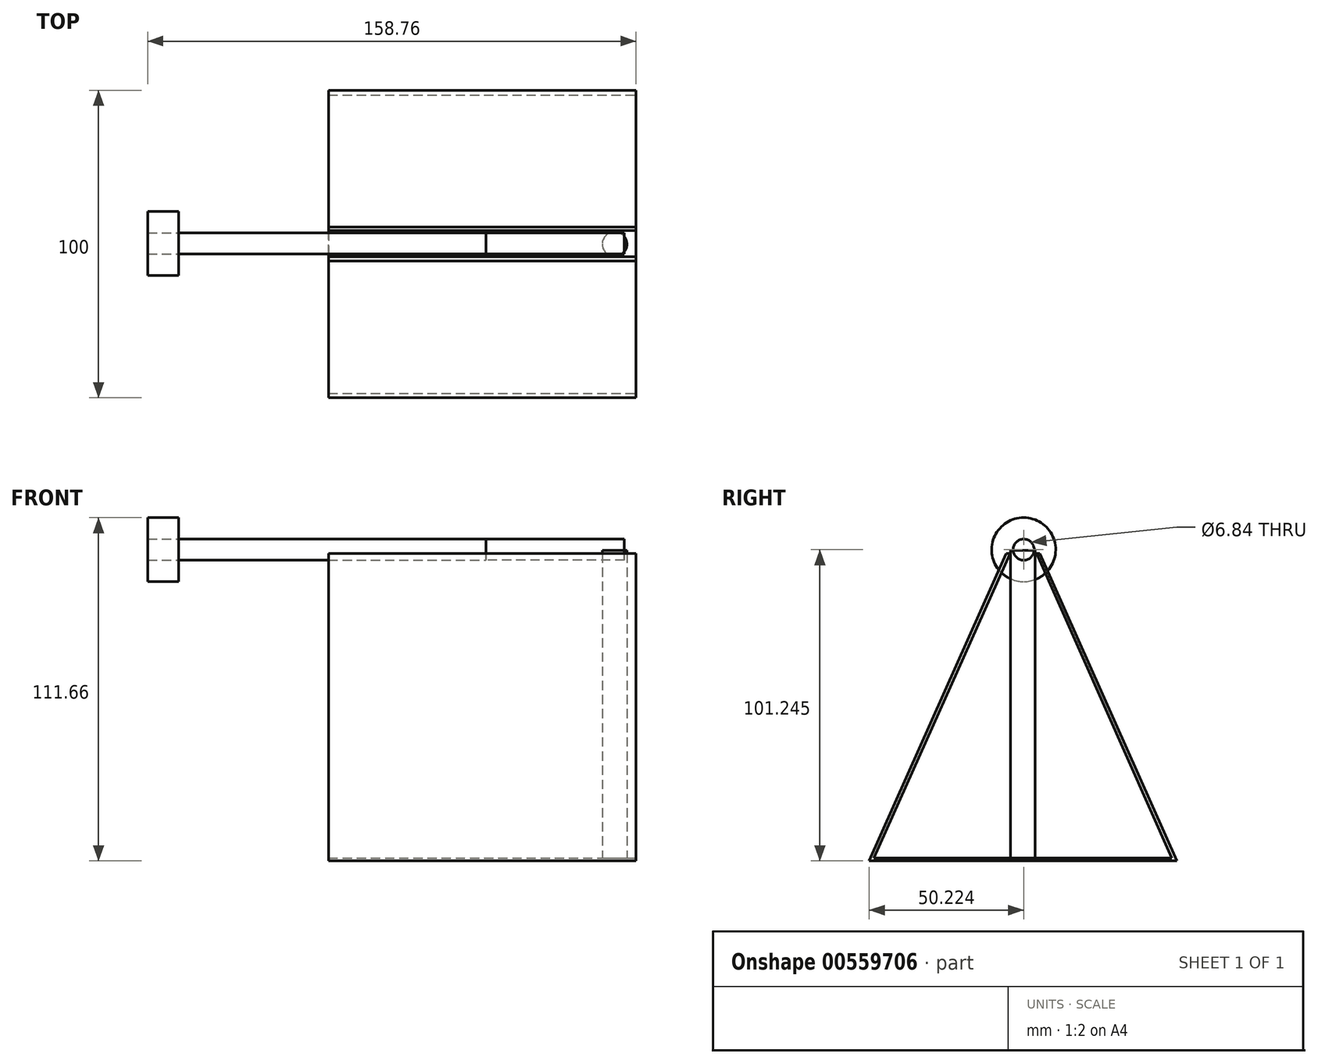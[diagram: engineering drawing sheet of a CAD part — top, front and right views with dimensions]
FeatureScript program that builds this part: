
annotation { "Feature Type Name" : "Feature", "Feature Type Description" : "" }
export const myFeature = defineFeature(function(context is Context, id is Id, definition is map)
    precondition{}
    {
        {
            var Q0;
            Q0=qCreatedBy(makeId("Front.planeOp"),FACE);
            var sketch = newSketch(context, id + "F0", { "sketchPlane" : qUnion([Q0])});
            skLineSegment(sketch, "E0.bottom", {"start": v(-51.24, 0) * mm, "end": v(48.76, 0) * mm});
            skLineSegment(sketch, "E0.top", {"start": v(-51.24, 100) * mm, "end": v(48.76, 100) * mm});
            skLineSegment(sketch, "E0.left", {"start": v(-51.24, 0) * mm, "end": v(-51.24, 100) * mm});
            skLineSegment(sketch, "E0.right", {"start": v(48.76, 0) * mm, "end": v(48.76, 100) * mm});
            skSolve(sketch);
        }
        {
            var Q0;
            Q0=makeQuery(id+"F0.imprint","IMPRINT",FACE,{"disambiguationData":[TD([[makeQuery(id+"F0.imprint","IMPRINT",EDGE,{"derivedFrom":sQuery(id+"F0.wireOp",EDGE,"E0.bottom")}),1.0]])]});
            extrude(context, id + "F1", {"entities" : qUnion([Q0]), "oppositeDirection" : true, "depth" : 100 * mm, "offsetDistance" : 25 * mm});
        }
        {
            var Q0;
            Q0=makeQuery(id+"F1.opExtrude","SWEPT_FACE",FACE,{"disambiguationData":[OSD([sQuery(id+"F0.wireOp",EDGE,"E0.right")])]});
            var sketch = newSketch(context, id + "F2", { "sketchPlane" : qUnion([Q0])});
            skLineSegment(sketch, "E1", {"start": v(0, 0) * mm, "end": v(100, 0) * mm, "construction": true});
            skLineSegment(sketch, "E2", {"start": v(100, 0) * mm, "end": v(50, 0) * mm, "construction": true});
            skLineSegment(sketch, "E3", {"start": v(50, 0) * mm, "end": v(50, 100) * mm, "construction": true});
            skLineSegment(sketch, "E4", {"start": v(0, 50) * mm, "end": v(100, 50) * mm, "construction": true});
            skLineSegment(sketch, "E5", {"start": v(50, 100) * mm, "end": v(44.5, 100) * mm, "construction": true});
            skLineSegment(sketch, "E6", {"start": v(50, 100) * mm, "end": v(55.5, 100) * mm, "construction": true});
            skLineSegment(sketch, "E7", {"start": v(0, 0) * mm, "end": v(44.5, 100) * mm});
            skLineSegment(sketch, "E8", {"start": v(100, 0) * mm, "end": v(55.5, 100) * mm});
            skLineSegment(sketch, "E9", {"start": v(0, 0) * mm, "end": v(100, 0) * mm});
            skLineSegment(sketch, "E10", {"start": v(55.5, 100) * mm, "end": v(44.5, 100) * mm});
            skLineSegment(sketch, "E11", {"start": v(50, 100) * mm, "end": v(47.25, 100) * mm, "construction": true});
            skSolve(sketch);
        }
        {
            var Q0;
            {var subQ0=sQuery(id+"F2.wireOp",EDGE,"E7");Q0=makeQuery(id+"F2.imprint","IMPRINT",FACE,{"disambiguationData":[TD([[makeQuery(id+"F2.imprint","IMPRINT",EDGE,{"derivedFrom":subQ0}),1.0]])]});}
            var Q1;
            {var subQ0=sQuery(id+"F2.wireOp",EDGE,"E8");Q1=makeQuery(id+"F2.imprint","IMPRINT",FACE,{"disambiguationData":[TD([[makeQuery(id+"F2.imprint","IMPRINT",EDGE,{"derivedFrom":subQ0}),-1.0]])]});}
            extrude(context, id + "F3", {"entities" : qUnion([Q0, Q1]), "operationType" : NewBodyOperationType.REMOVE, "endBound" : BoundingType.THROUGH_ALL, "oppositeDirection" : true, "depth" : 25 * mm, "offsetDistance" : 25 * mm});
        }
        {
            var Q0;
            Q0=makeQuery(id+"F1.opExtrude","SWEPT_FACE",FACE,{"disambiguationData":[OSD([sQuery(id+"F0.wireOp",EDGE,"E0.right")])]});
            var sketch = newSketch(context, id + "F4", { "sketchPlane" : qUnion([Q0])});
            skLineSegment(sketch, "E12", {"start": v(4.83, 1) * mm, "end": v(98.46, 1) * mm});
            skLineSegment(sketch, "E13", {"start": v(98.46, 1) * mm, "end": v(54.4, 100) * mm});
            skLineSegment(sketch, "E14", {"start": v(54.4, 100) * mm, "end": v(45.81, 100) * mm});
            skLineSegment(sketch, "E15", {"start": v(4.83, 1) * mm, "end": v(1.43, 1) * mm});
            skLineSegment(sketch, "E16", {"start": v(1.43, 1) * mm, "end": v(45.81, 100) * mm});
            skSolve(sketch);
        }
        {
            var Q0;
            Q0=makeQuery(id+"F4.imprint","IMPRINT",FACE,{"disambiguationData":[TD([[makeQuery(id+"F4.imprint","IMPRINT",EDGE,{"derivedFrom":sQuery(id+"F4.wireOp",EDGE,"E12")}),1.0]])]});
            extrude(context, id + "F5", {"entities" : qUnion([Q0]), "operationType" : NewBodyOperationType.REMOVE, "endBound" : BoundingType.THROUGH_ALL, "oppositeDirection" : true, "depth" : 25 * mm, "offsetDistance" : 25 * mm});
        }
        {
            var Q0;
            Q0=makeQuery(id+"F5.boolean.opBoolean","COPY",FACE,{"derivedFrom":makeQuery(id+"F5.opExtrude","SWEPT_FACE",FACE,{"disambiguationData":[OSD([sQuery(id+"F4.wireOp",EDGE,"E12"),sQuery(id+"F4.wireOp",EDGE,"E15")])]})});
            var sketch = newSketch(context, id + "F6", { "sketchPlane" : qUnion([Q0])});
            skCircle(sketch, "E17", {"center": v(41.8, 49.94) * mm, "radius": 4 * mm});
            skPoint(sketch, "E17.centerSnap0", {"position": v(48.76, 49.94) * mm});
            skSolve(sketch);
        }
        {
            var Q0;
            Q0=makeQuery(id+"F6.imprint","IMPRINT",FACE,{"disambiguationData":[TD([[makeQuery(id+"F6.imprint","IMPRINT",EDGE,{"derivedFrom":sQuery(id+"F6.wireOp",EDGE,"E17")}),1.0]])]});
            extrude(context, id + "F7", {"entities" : qUnion([Q0]), "operationType" : NewBodyOperationType.ADD, "depth" : 100 * mm, "offsetDistance" : 25 * mm});
        }
        {
            var Q0;
            Q0=qCreatedBy(makeId("Right.planeOp"),FACE);
            var sketch = newSketch(context, id + "F8", { "sketchPlane" : qUnion([Q0])});
            skCircle(sketch, "E18", {"center": v(50.22, 101.25) * mm, "radius": 3.42 * mm});
            skSolve(sketch);
        }
        {
            var Q0;
            Q0=makeQuery(id+"F8.imprint","IMPRINT",FACE,{"disambiguationData":[TD([[makeQuery(id+"F8.imprint","IMPRINT",EDGE,{"derivedFrom":sQuery(id+"F8.wireOp",EDGE,"E18")}),1.0]])]});
            extrude(context, id + "F9", {"entities" : qUnion([Q0]), "oppositeDirection" : true, "depth" : 100 * mm, "offsetDistance" : 25 * mm});
        }
        {
            var Q0;
            Q0=makeQuery(id+"F9.opExtrude","CAP_FACE",FACE,{"disambiguationData":[OSD([sQuery(id+"F8.wireOp",EDGE,"E18")])],"isStart":true});
            extrude(context, id + "F10", {"entities" : qUnion([Q0]), "depth" : 45 * mm, "offsetDistance" : 25 * mm});
        }
        {
            var Q0;
            Q0=makeQuery(id+"F9.opExtrude","CAP_FACE",FACE,{"disambiguationData":[OSD([sQuery(id+"F8.wireOp",EDGE,"E18")])],"isStart":false});
            var sketch = newSketch(context, id + "F11", { "sketchPlane" : qUnion([Q0])});
            skCircle(sketch, "E19", {"center": v(-50.22, 101.25) * mm, "radius": 10.41 * mm});
            skSolve(sketch);
        }
        {
            var Q0;
            Q0=makeQuery(id+"F11.imprint","IMPRINT",FACE,{"disambiguationData":[TD([[makeQuery(id+"F11.imprint","IMPRINT",EDGE,{"derivedFrom":sQuery(id+"F11.wireOp",EDGE,"E19")}),1.0]])]});
            extrude(context, id + "F12", {"entities" : qUnion([Q0]), "depth" : 10 * mm, "offsetDistance" : 25 * mm});
        }
    });
